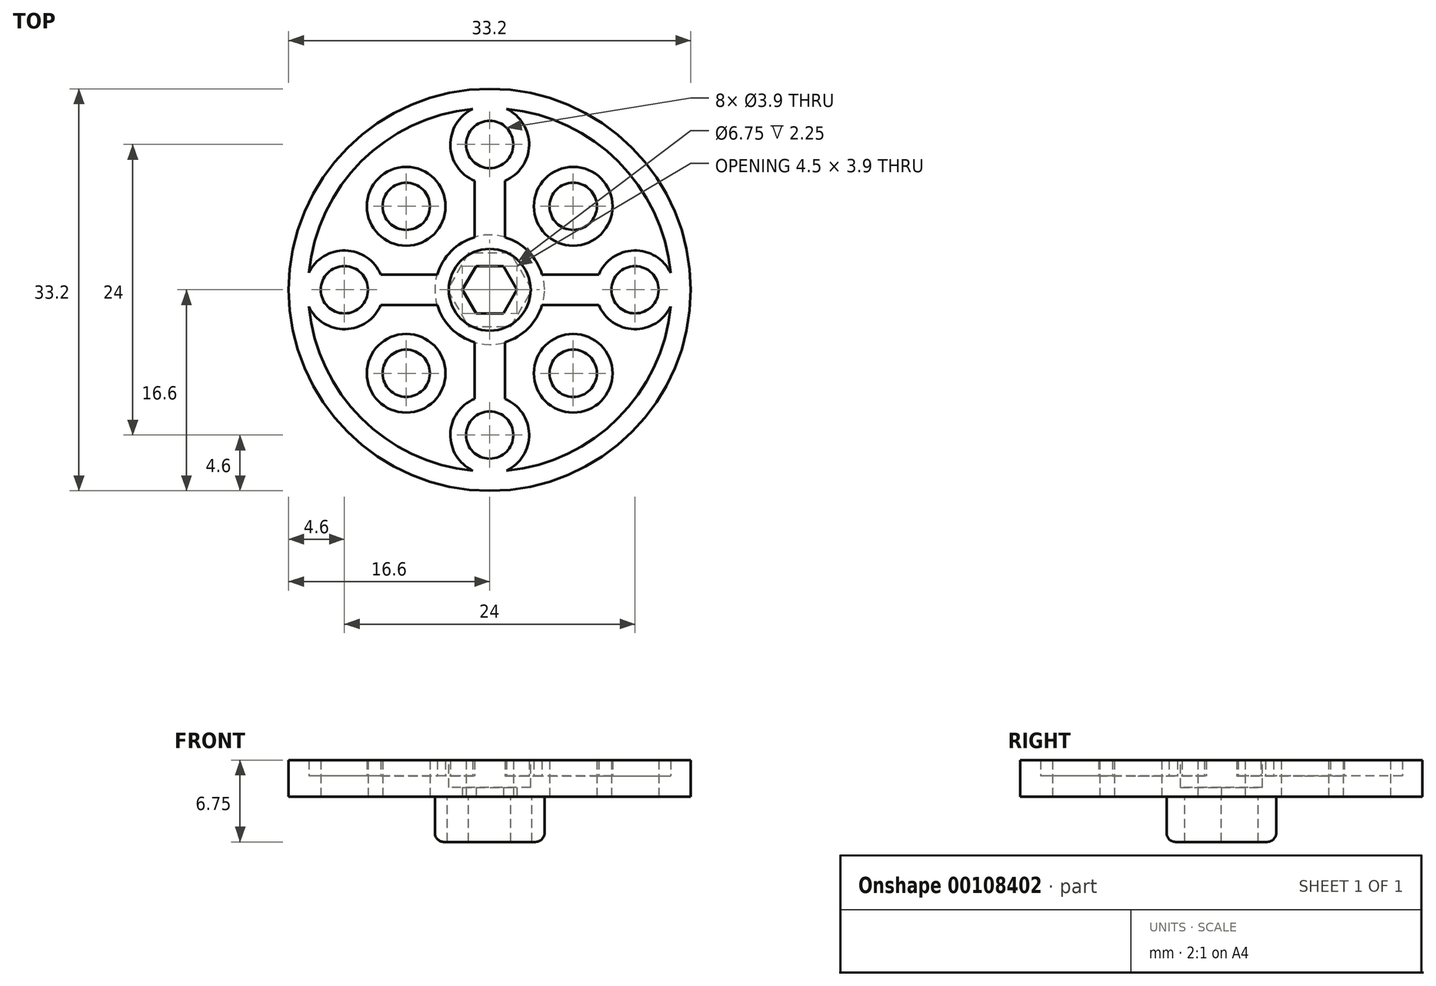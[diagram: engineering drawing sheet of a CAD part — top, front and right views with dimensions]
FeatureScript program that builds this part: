
annotation { "Feature Type Name" : "Feature", "Feature Type Description" : "" }
export const myFeature = defineFeature(function(context is Context, id is Id, definition is map)
    precondition{}
    {
        {
            var Q0;
            Q0=qCreatedBy(makeId("Top.planeOp"),FACE);
            var sketch = newSketch(context, id + "F0", { "sketchPlane" : qUnion([Q0])});
            skCircle(sketch, "E0", {"center": v(0, 0) * mm, "radius": 15 * mm});
            skCircle(sketch, "E1", {"center": v(6.9, 6.9) * mm, "radius": 1.95 * mm});
            skCircle(sketch, "E2", {"center": v(6.9, 6.9) * mm, "radius": 3.25 * mm});
            skCircle(sketch, "E3.1.0", {"center": v(-6.9, 6.9) * mm, "radius": 3.25 * mm});
            skCircle(sketch, "E3.1.1", {"center": v(-6.9, 6.9) * mm, "radius": 1.95 * mm});
            skCircle(sketch, "E3.2.0", {"center": v(-6.9, -6.9) * mm, "radius": 3.25 * mm});
            skCircle(sketch, "E3.2.1", {"center": v(-6.9, -6.9) * mm, "radius": 1.95 * mm});
            skCircle(sketch, "E3.3.0", {"center": v(6.9, -6.9) * mm, "radius": 3.25 * mm});
            skCircle(sketch, "E3.3.1", {"center": v(6.9, -6.9) * mm, "radius": 1.95 * mm});
            skCircle(sketch, "E4", {"center": v(0, 12) * mm, "radius": 1.95 * mm});
            skArc(sketch, "E5", {"start": v(-1.4, 14.93) * mm, "mid": v(0, 8.75) * mm, "end": v(1.4, 14.93) * mm});
            skCircle(sketch, "E6", {"center": v(0, 0) * mm, "radius": 16.6 * mm});
            skLineSegment(sketch, "E7", {"start": v(0, 0) * mm, "end": v(0, 0) * mm});
            skCircle(sketch, "E8.1.0", {"center": v(-12, 0) * mm, "radius": 1.95 * mm});
            skArc(sketch, "E8.1.1", {"start": v(-14.93, -1.4) * mm, "mid": v(-8.75, 0) * mm, "end": v(-14.93, 1.4) * mm});
            skCircle(sketch, "E8.2.0", {"center": v(0, -12) * mm, "radius": 1.95 * mm});
            skArc(sketch, "E8.2.1", {"start": v(1.4, -14.93) * mm, "mid": v(0, -8.75) * mm, "end": v(-1.4, -14.93) * mm});
            skCircle(sketch, "E8.3.0", {"center": v(12, 0) * mm, "radius": 1.95 * mm});
            skArc(sketch, "E8.3.1", {"start": v(14.93, 1.4) * mm, "mid": v(8.75, 0) * mm, "end": v(14.93, -1.4) * mm});
            skLineSegment(sketch, "E9", {"start": v(-16.6, 0) * mm, "end": v(-15, 0) * mm});
            skCircle(sketch, "E10", {"center": v(0, 0) * mm, "radius": 3.38 * mm});
            skCircle(sketch, "E11", {"center": v(0, 0) * mm, "radius": 4.5 * mm});
            skCircle(sketch, "E12.cCircle", {"center": v(0, 0) * mm, "radius": 1.95 * mm, "construction": true});
            skLineSegment(sketch, "E12.0", {"start": v(-1.13, 1.95) * mm, "end": v(1.13, 1.95) * mm});
            skLineSegment(sketch, "E12.1", {"start": v(1.12, 1.95) * mm, "end": v(2.25, 0) * mm});
            skLineSegment(sketch, "E12.2", {"start": v(2.25, 0) * mm, "end": v(1.13, -1.95) * mm});
            skLineSegment(sketch, "E12.3", {"start": v(1.13, -1.95) * mm, "end": v(-1.12, -1.95) * mm});
            skLineSegment(sketch, "E12.4", {"start": v(-1.12, -1.95) * mm, "end": v(-2.25, 0) * mm});
            skLineSegment(sketch, "E12.5", {"start": v(-2.25, 0) * mm, "end": v(-1.13, 1.95) * mm});
            skPoint(sketch, "E12.0.midPoint", {"position": v(0, 1.95) * mm});
            skLineSegment(sketch, "E13", {"start": v(6, 1.25) * mm, "end": v(4.32, 1.25) * mm});
            skLineSegment(sketch, "E14", {"start": v(6, 1.25) * mm, "end": v(9, 1.25) * mm});
            skLineSegment(sketch, "E15.MirrorCS", {"start": v(9, -1.25) * mm, "end": v(4.32, -1.25) * mm});
            skLineSegment(sketch, "E16.1.2", {"start": v(-1.25, 6) * mm, "end": v(-1.25, 9) * mm});
            skLineSegment(sketch, "E16.1.3", {"start": v(1.25, 9) * mm, "end": v(1.25, 4.32) * mm});
            skLineSegment(sketch, "E16.1.4", {"start": v(-1.25, 6) * mm, "end": v(-1.25, 4.32) * mm});
            skLineSegment(sketch, "E16.2.2", {"start": v(-6, -1.25) * mm, "end": v(-9, -1.25) * mm});
            skLineSegment(sketch, "E16.2.3", {"start": v(-9, 1.25) * mm, "end": v(-4.32, 1.25) * mm});
            skLineSegment(sketch, "E16.2.4", {"start": v(-6, -1.25) * mm, "end": v(-4.32, -1.25) * mm});
            skLineSegment(sketch, "E17.6.3.0", {"start": v(1.25, -6) * mm, "end": v(1.25, -9) * mm});
            skLineSegment(sketch, "E17.9.3.0", {"start": v(-1.25, -9) * mm, "end": v(-1.25, -4.32) * mm});
            skLineSegment(sketch, "E17.12.3.0", {"start": v(1.25, -6) * mm, "end": v(1.25, -4.32) * mm});
            skSolve(sketch);
        }
        {
            var Q0;
            Q0 = qSketchRegion(id + "F0", true);
            var Q1;
            {var subQ3=sQuery(id+"F0.wireOp",EDGE,"wVo0opY1-z610-xm1O-ogbB-GxVFeKAdTOKm.left");var subQ6=sQuery(id+"F0.wireOp",EDGE,"E5");var subQ9=makeQuery(id+"F0.imprint","INTERSECT",VERTEX,{"derivedFrom":[subQ6,subQ3]});Q1=makeQuery(id+"F0.imprint","IMPRINT",FACE,{"disambiguationData":[TD([[makeQuery(id+"F0.imprint","IMPRINT",EDGE,{"disambiguationData":[TD([[subQ9,-1.0]])],"derivedFrom":subQ6}),-1.0]])]});}
            var Q2;
            {var subQ5=sQuery(id+"F0.wireOp",EDGE,"E8.2.2");var subQ6=sQuery(id+"F0.wireOp",EDGE,"wVo0opY1-z610-xm1O-ogbB-GxVFeKAdTOKm.right");var subQ7=makeQuery(id+"F0.imprint","INTERSECT",VERTEX,{"derivedFrom":[subQ6,subQ5]});Q2=makeQuery(id+"F0.imprint","IMPRINT",FACE,{"disambiguationData":[TD([[makeQuery(id+"F0.imprint","IMPRINT",EDGE,{"disambiguationData":[TD([[subQ7,-1.0]])],"derivedFrom":subQ6}),1.0]])]});}
            var Q3;
            {var subQ5=sQuery(id+"F0.wireOp",EDGE,"E8.2.2");var subQ6=sQuery(id+"F0.wireOp",EDGE,"wVo0opY1-z610-xm1O-ogbB-GxVFeKAdTOKm.right");var subQ7=makeQuery(id+"F0.imprint","INTERSECT",VERTEX,{"derivedFrom":[subQ6,subQ5]});Q3=makeQuery(id+"F0.imprint","IMPRINT",FACE,{"disambiguationData":[TD([[makeQuery(id+"F0.imprint","IMPRINT",EDGE,{"disambiguationData":[TD([[subQ7,-1.0]])],"derivedFrom":subQ6}),-1.0]])]});}
            var Q4;
            {var subQ3=sQuery(id+"F0.wireOp",EDGE,"E8.1.1");var subQ5=sQuery(id+"F0.wireOp",EDGE,"E8.1.2");var subQ6=makeQuery(id+"F0.imprint","INTERSECT",VERTEX,{"derivedFrom":[subQ3,subQ5]});Q4=makeQuery(id+"F0.imprint","IMPRINT",FACE,{"disambiguationData":[TD([[makeQuery(id+"F0.imprint","IMPRINT",EDGE,{"disambiguationData":[TD([[subQ6,-1.0]])],"derivedFrom":subQ3}),-1.0]])]});}
            var Q5;
            {var subQ3=sQuery(id+"F0.wireOp",EDGE,"E8.1.3");var subQ5=sQuery(id+"F0.wireOp",EDGE,"E8.1.1");var subQ6=makeQuery(id+"F0.imprint","INTERSECT",VERTEX,{"derivedFrom":[subQ5,subQ3]});Q5=makeQuery(id+"F0.imprint","IMPRINT",FACE,{"disambiguationData":[TD([[makeQuery(id+"F0.imprint","IMPRINT",EDGE,{"disambiguationData":[TD([[subQ6,1.0]])],"derivedFrom":subQ5}),-1.0]])]});}
            var Q6;
            Q6=makeQuery(id+"F0.imprint","IMPRINT",FACE,{"disambiguationData":[TD([[makeQuery(id+"F0.imprint","IMPRINT",EDGE,{"derivedFrom":sQuery(id+"F0.wireOp",EDGE,"E3.1.0")}),1.0]])]});
            var Q7;
            Q7=makeQuery(id+"F0.imprint","IMPRINT",FACE,{"disambiguationData":[TD([[makeQuery(id+"F0.imprint","IMPRINT",EDGE,{"derivedFrom":sQuery(id+"F0.wireOp",EDGE,"E4")}),-1.0]])]});
            var Q8;
            Q8=makeQuery(id+"F0.imprint","IMPRINT",FACE,{"disambiguationData":[TD([[makeQuery(id+"F0.imprint","IMPRINT",EDGE,{"derivedFrom":sQuery(id+"F0.wireOp",EDGE,"E1")}),-1.0]])]});
            var Q9;
            Q9=makeQuery(id+"F0.imprint","IMPRINT",FACE,{"disambiguationData":[TD([[makeQuery(id+"F0.imprint","IMPRINT",EDGE,{"derivedFrom":sQuery(id+"F0.wireOp",EDGE,"E8.3.0")}),-1.0]])]});
            var Q10;
            Q10=makeQuery(id+"F0.imprint","IMPRINT",FACE,{"disambiguationData":[TD([[makeQuery(id+"F0.imprint","IMPRINT",EDGE,{"derivedFrom":sQuery(id+"F0.wireOp",EDGE,"E3.3.0")}),1.0]])]});
            var Q11;
            Q11=makeQuery(id+"F0.imprint","IMPRINT",FACE,{"disambiguationData":[TD([[makeQuery(id+"F0.imprint","IMPRINT",EDGE,{"derivedFrom":sQuery(id+"F0.wireOp",EDGE,"E8.2.0")}),-1.0]])]});
            var Q12;
            Q12=makeQuery(id+"F0.imprint","IMPRINT",FACE,{"disambiguationData":[TD([[makeQuery(id+"F0.imprint","IMPRINT",EDGE,{"derivedFrom":sQuery(id+"F0.wireOp",EDGE,"E3.2.0")}),1.0]])]});
            var Q13;
            {var subQ1=sQuery(id+"F0.wireOp",EDGE,"JebTKTrF-ul0E-zG5r-YUPd-CZcp4a8UYJNf");var subQ4=sQuery(id+"F0.wireOp",EDGE,"E0");var subQ5=makeQuery(id+"F0.imprint","INTERSECT",VERTEX,{"derivedFrom":[subQ4,subQ1]});Q13=makeQuery(id+"F0.imprint","IMPRINT",FACE,{"disambiguationData":[TD([[makeQuery(id+"F0.imprint","IMPRINT",EDGE,{"disambiguationData":[TD([[subQ5,-1.0]])],"derivedFrom":subQ4}),1.0]])]});}
            var Q14;
            {var subQ1=sQuery(id+"F0.wireOp",EDGE,"JebTKTrF-ul0E-zG5r-YUPd-CZcp4a8UYJNf");var subQ4=sQuery(id+"F0.wireOp",EDGE,"E0");var subQ5=makeQuery(id+"F0.imprint","INTERSECT",VERTEX,{"derivedFrom":[subQ4,subQ1]});Q14=makeQuery(id+"F0.imprint","IMPRINT",FACE,{"disambiguationData":[TD([[makeQuery(id+"F0.imprint","IMPRINT",EDGE,{"disambiguationData":[TD([[subQ5,1.0]])],"derivedFrom":subQ4}),1.0]])]});}
            var Q15;
            Q15=makeQuery(id+"F0.imprint","IMPRINT",FACE,{"disambiguationData":[TD([[makeQuery(id+"F0.imprint","IMPRINT",EDGE,{"derivedFrom":sQuery(id+"F0.wireOp",EDGE,"E8.1.0")}),-1.0]])]});
            var Q16;
            Q16=makeQuery(id+"F0.imprint","IMPRINT",FACE,{"disambiguationData":[TD([[makeQuery(id+"F0.imprint","IMPRINT",EDGE,{"derivedFrom":sQuery(id+"F0.wireOp",EDGE,"E10")}),-1.0]])]});
            var Q17;
            {var subQ0=sQuery(id+"F0.wireOp",EDGE,"E8.3.2");Q17=makeQuery(id+"F0.imprint","IMPRINT",FACE,{"disambiguationData":[TD([[makeQuery(id+"F0.imprint","IMPRINT",EDGE,{"derivedFrom":subQ0}),-1.0]])]});}
            var Q18;
            {var subQ0=sQuery(id+"F0.wireOp",EDGE,"E8.2.2");Q18=makeQuery(id+"F0.imprint","IMPRINT",FACE,{"disambiguationData":[TD([[makeQuery(id+"F0.imprint","IMPRINT",EDGE,{"derivedFrom":subQ0}),-1.0]])]});}
            var Q19;
            Q19=makeQuery(id+"F0.imprint","IMPRINT",FACE,{"disambiguationData":[TD([[makeQuery(id+"F0.imprint","IMPRINT",EDGE,{"derivedFrom":sQuery(id+"F0.wireOp",EDGE,"E10")}),1.0]])]});
            var Q20;
            {var subQ1=sQuery(id+"F0.wireOp",EDGE,"E13");Q20=makeQuery(id+"F0.imprint","IMPRINT",FACE,{"disambiguationData":[TD([[makeQuery(id+"F0.imprint","IMPRINT",EDGE,{"derivedFrom":subQ1}),1.0]])]});}
            var Q21;
            {var subQ3=sQuery(id+"F0.wireOp",EDGE,"E17.6.3.0");Q21=makeQuery(id+"F0.imprint","IMPRINT",FACE,{"disambiguationData":[TD([[makeQuery(id+"F0.imprint","IMPRINT",EDGE,{"derivedFrom":subQ3}),-1.0]])]});}
            extrude(context, id + "F1", {"entities" : qUnion([Q0, Q1, Q2, Q3, Q4, Q5, Q6, Q7, Q8, Q9, Q10, Q11, Q12, Q13, Q14, Q15, Q16, Q17, Q18, Q19, Q20, Q21]), "depth" : 3 * mm});
        }
        {
            var Q0;
            Q0=makeQuery(id+"F0.imprint","IMPRINT",FACE,{"disambiguationData":[TD([[makeQuery(id+"F0.imprint","IMPRINT",EDGE,{"derivedFrom":sQuery(id+"F0.wireOp",EDGE,"E3.1.0")}),-1.0]])]});
            var Q1;
            Q1=makeQuery(id+"F0.imprint","IMPRINT",FACE,{"disambiguationData":[TD([[makeQuery(id+"F0.imprint","IMPRINT",EDGE,{"derivedFrom":sQuery(id+"F0.wireOp",EDGE,"E2")}),-1.0]])]});
            var Q2;
            Q2=makeQuery(id+"F0.imprint","IMPRINT",FACE,{"disambiguationData":[TD([[makeQuery(id+"F0.imprint","IMPRINT",EDGE,{"derivedFrom":sQuery(id+"F0.wireOp",EDGE,"E3.3.0")}),-1.0]])]});
            var Q3;
            Q3=makeQuery(id+"F0.imprint","IMPRINT",FACE,{"disambiguationData":[TD([[makeQuery(id+"F0.imprint","IMPRINT",EDGE,{"derivedFrom":sQuery(id+"F0.wireOp",EDGE,"E3.2.0")}),-1.0]])]});
            var Q4;
            Q4=makeQuery(id+"F0.imprint","IMPRINT",FACE,{"disambiguationData":[TD([[makeQuery(id+"F0.imprint","IMPRINT",EDGE,{"derivedFrom":sQuery(id+"F0.wireOp",EDGE,"E10")}),1.0]])]});
            extrude(context, id + "F2", {"entities" : qUnion([Q0, Q1, Q2, Q3, Q4]), "operationType" : NewBodyOperationType.ADD, "depth" : (3 - 1.3) * mm});
        }
        {
            var Q0;
            Q0 = qSketchRegion(id + "F0", true);
            var Q1;
            Q1=makeQuery(id+"F2.opExtrude","CAP_FACE",FACE,{"disambiguationData":[OSD([sQuery(id+"F0.wireOp",EDGE,"E10"),sQuery(id+"F0.wireOp",EDGE,"E12.0"),sQuery(id+"F0.wireOp",EDGE,"E12.1"),sQuery(id+"F0.wireOp",EDGE,"E12.2"),sQuery(id+"F0.wireOp",EDGE,"E12.3"),sQuery(id+"F0.wireOp",EDGE,"E12.4"),sQuery(id+"F0.wireOp",EDGE,"E12.5")])],"isStart":false});
            extrude(context, id + "F3", {"entities" : qUnion([Q0, Q1]), "operationType" : NewBodyOperationType.ADD, "depth" : 3 * mm});
        }
        {
            var Q0;
            Q0=makeQuery(id+"F1.opExtrude","CAP_FACE",FACE,{"disambiguationData":[OSD([sQuery(id+"F0.wireOp",EDGE,"E0"),sQuery(id+"F0.wireOp",EDGE,"E4"),sQuery(id+"F0.wireOp",EDGE,"E5"),sQuery(id+"F0.wireOp",EDGE,"wVo0opY1-z610-xm1O-ogbB-GxVFeKAdTOKm.left"),sQuery(id+"F0.wireOp",EDGE,"E6"),sQuery(id+"F0.wireOp",EDGE,"E8.1.0"),sQuery(id+"F0.wireOp",EDGE,"E8.1.1"),sQuery(id+"F0.wireOp",EDGE,"E8.1.2"),sQuery(id+"F0.wireOp",EDGE,"E8.1.3"),sQuery(id+"F0.wireOp",EDGE,"E8.2.0"),sQuery(id+"F0.wireOp",EDGE,"E8.2.1"),sQuery(id+"F0.wireOp",EDGE,"E8.2.2"),sQuery(id+"F0.wireOp",EDGE,"E8.2.3"),sQuery(id+"F0.wireOp",EDGE,"E8.3.0"),sQuery(id+"F0.wireOp",EDGE,"E8.3.1"),sQuery(id+"F0.wireOp",EDGE,"E8.3.2"),sQuery(id+"F0.wireOp",EDGE,"E11"),sQuery(id+"F0.wireOp",EDGE,"7fa01f5f-1f3f-4dcd-8827-d373d467dbf4.trimOffspring"),sQuery(id+"F0.wireOp",EDGE,"e1f0f182-a094-4c4d-9390-e69cab6e19e0.trimOffspring"),sQuery(id+"F0.wireOp",EDGE,"E12.0"),sQuery(id+"F0.wireOp",EDGE,"E12.1"),sQuery(id+"F0.wireOp",EDGE,"E12.2"),sQuery(id+"F0.wireOp",EDGE,"E12.3"),sQuery(id+"F0.wireOp",EDGE,"E12.4"),sQuery(id+"F0.wireOp",EDGE,"E12.5")])],"isStart":false});
            var sketch = newSketch(context, id + "F4", { "sketchPlane" : qUnion([Q0])});
            skCircle(sketch, "E18", {"center": v(0, 0) * mm, "radius": 3.38 * mm});
            skSolve(sketch);
        }
        {
            var Q0;
            Q0=makeQuery(id+"F4.imprint","IMPRINT",FACE,{"disambiguationData":[TD([[makeQuery(id+"F4.imprint","IMPRINT",EDGE,{"derivedFrom":sQuery(id+"F4.wireOp",EDGE,"E18")}),1.0]])]});
            extrude(context, id + "F5", {"entities" : qUnion([Q0]), "operationType" : NewBodyOperationType.REMOVE, "oppositeDirection" : true, "depth" : 2.25 * mm});
        }
        {
            var Q0;
            {var subQ0=sQuery(id+"F0.wireOp",EDGE,"E17.12.3.0");var subQ1=sQuery(id+"F0.wireOp",EDGE,"E17.6.3.0");var subQ2=sQuery(id+"F0.wireOp",EDGE,"E15.MirrorCS");var subQ3=sQuery(id+"F0.wireOp",EDGE,"E11");var subQ4=sQuery(id+"F0.wireOp",EDGE,"E8.3.1");var subQ5=sQuery(id+"F0.wireOp",EDGE,"E8.2.1");var subQ6=sQuery(id+"F0.wireOp",EDGE,"E3.3.0");var subQ7=sQuery(id+"F0.wireOp",EDGE,"E0");var subQ8=sQuery(id+"F0.wireOp",EDGE,"E17.9.3.0");var subQ9=sQuery(id+"F0.wireOp",EDGE,"E16.2.4");var subQ10=sQuery(id+"F0.wireOp",EDGE,"E16.2.2");var subQ11=sQuery(id+"F0.wireOp",EDGE,"E8.1.1");var subQ12=sQuery(id+"F0.wireOp",EDGE,"E3.2.0");var subQ13=sQuery(id+"F0.wireOp",EDGE,"E16.2.3");var subQ14=sQuery(id+"F0.wireOp",EDGE,"E16.1.4");var subQ15=sQuery(id+"F0.wireOp",EDGE,"E16.1.2");var subQ16=sQuery(id+"F0.wireOp",EDGE,"E5");var subQ17=sQuery(id+"F0.wireOp",EDGE,"E3.1.0");var subQ18=sQuery(id+"F0.wireOp",EDGE,"E16.1.3");var subQ19=sQuery(id+"F0.wireOp",EDGE,"E14");var subQ20=sQuery(id+"F0.wireOp",EDGE,"E13");var subQ21=sQuery(id+"F0.wireOp",EDGE,"E2");Q0=makeQuery(id+"F2.boolean.opBoolean","MERGE",FACE,{"derivedFrom":[makeQuery(id+"F1.opExtrude","CAP_FACE",FACE,{"disambiguationData":[OSD([subQ7,sQuery(id+"F0.wireOp",EDGE,"E4"),subQ16,sQuery(id+"F0.wireOp",EDGE,"E6"),sQuery(id+"F0.wireOp",EDGE,"E8.1.0"),subQ11,sQuery(id+"F0.wireOp",EDGE,"E8.2.0"),subQ5,sQuery(id+"F0.wireOp",EDGE,"E8.3.0"),subQ4,subQ3,sQuery(id+"F0.wireOp",EDGE,"E12.0"),sQuery(id+"F0.wireOp",EDGE,"E12.1"),sQuery(id+"F0.wireOp",EDGE,"E12.2"),sQuery(id+"F0.wireOp",EDGE,"E12.3"),sQuery(id+"F0.wireOp",EDGE,"E12.4"),sQuery(id+"F0.wireOp",EDGE,"E12.5"),subQ20,subQ19,subQ2,subQ15,subQ18,subQ14,subQ10,subQ13,subQ9,subQ1,subQ8,subQ0])],"isStart":true}),makeQuery(id+"F1.opExtrude","CAP_FACE",FACE,{"disambiguationData":[OSD([sQuery(id+"F0.wireOp",EDGE,"E1"),subQ21])],"isStart":true}),makeQuery(id+"F1.opExtrude","CAP_FACE",FACE,{"disambiguationData":[OSD([subQ17,sQuery(id+"F0.wireOp",EDGE,"E3.1.1")])],"isStart":true}),makeQuery(id+"F1.opExtrude","CAP_FACE",FACE,{"disambiguationData":[OSD([subQ12,sQuery(id+"F0.wireOp",EDGE,"E3.2.1")])],"isStart":true}),makeQuery(id+"F1.opExtrude","CAP_FACE",FACE,{"disambiguationData":[OSD([subQ6,sQuery(id+"F0.wireOp",EDGE,"E3.3.1")])],"isStart":true}),makeQuery(id+"F2.opExtrude","CAP_FACE",FACE,{"disambiguationData":[OSD([subQ7,subQ21,subQ16,subQ4,subQ3,subQ20,subQ19,subQ18])],"isStart":true}),makeQuery(id+"F2.opExtrude","CAP_FACE",FACE,{"disambiguationData":[OSD([subQ7,subQ17,subQ16,subQ11,subQ3,subQ15,subQ14,subQ13])],"isStart":true}),makeQuery(id+"F2.opExtrude","CAP_FACE",FACE,{"disambiguationData":[OSD([subQ7,subQ12,subQ11,subQ5,subQ3,subQ10,subQ9,subQ8])],"isStart":true}),makeQuery(id+"F2.opExtrude","CAP_FACE",FACE,{"disambiguationData":[OSD([subQ7,subQ6,subQ5,subQ4,subQ3,subQ2,subQ1,subQ0])],"isStart":true})]});}
            var sketch = newSketch(context, id + "F6", { "sketchPlane" : qUnion([Q0])});
            skCircle(sketch, "E19", {"center": v(0, 0) * mm, "radius": 4.53 * mm});
            skCircle(sketch, "E20.cCircle", {"center": v(0, 0) * mm, "radius": 3.03 * mm, "construction": true});
            skPoint(sketch, "E20.cCircle.perimeterSnap0", {"position": v(0, 1.95) * mm});
            skLineSegment(sketch, "E20.0", {"start": v(-1.75, 3.03) * mm, "end": v(1.75, 3.03) * mm});
            skLineSegment(sketch, "E20.1", {"start": v(1.75, 3.03) * mm, "end": v(3.5, 0) * mm});
            skLineSegment(sketch, "E20.2", {"start": v(3.5, 0) * mm, "end": v(1.75, -3.03) * mm});
            skLineSegment(sketch, "E20.3", {"start": v(1.75, -3.03) * mm, "end": v(-1.75, -3.03) * mm});
            skLineSegment(sketch, "E20.4", {"start": v(-1.75, -3.03) * mm, "end": v(-3.5, 0) * mm});
            skLineSegment(sketch, "E20.5", {"start": v(-3.5, 0) * mm, "end": v(-1.75, 3.03) * mm});
            skPoint(sketch, "E20.0.midPoint", {"position": v(0, 3.03) * mm});
            skPoint(sketch, "E20.0.midPoint.positionSnap0", {"position": v(0, 1.95) * mm});
            skSolve(sketch);
        }
        {
            var Q0;
            Q0 = qSketchRegion(id + "F6", true);
            extrude(context, id + "F7", {"entities" : qUnion([Q0]), "operationType" : NewBodyOperationType.ADD, "depth" : 3.75 * mm});
        }
        {
            var Q0;
            Q0=makeQuery(id+"F7.opExtrude","CAP_EDGE",EDGE,{"disambiguationData":[OSD([sQuery(id+"F6.wireOp",EDGE,"E19")])],"isStart":false});
            fillet(context, id + "F8", {"entities" : qUnion([Q0]), "radius" : .75 * mm, "tangentPropagation" : true, "allowEdgeOverflow" : false});
        }
    });
